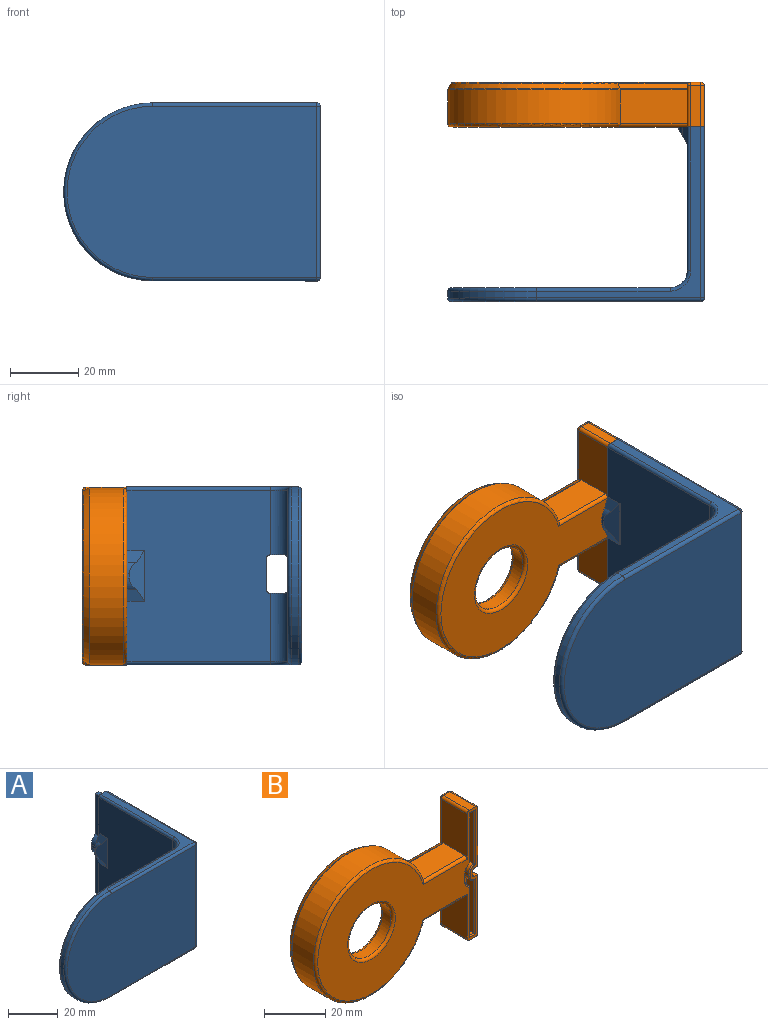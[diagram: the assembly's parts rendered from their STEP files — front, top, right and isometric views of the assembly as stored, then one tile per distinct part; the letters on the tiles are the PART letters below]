
ASSEMBLY  parts=2 mates=1
PART A: 74 faces, bbox 77.1x54.4x56.3 mm
  f0: plane 50x50mm, normal (1,0,0), area 2292.3mm2, adj f2,f6,f7,f11,f12,f13,f14,f18
  f1: plane 50x42mm, normal (-1,0,0), area 2013.4mm2, adj f11,f12,f13,f19,f22,f23,f24,f41
  f2: plane 74x50mm, normal (0,1,0), area 3023.7mm2, adj f0,f20,f21,f44,f45,f49,f50,f51
  f3: plane 73x50mm, normal (0,-1,0), area 3381.7mm2, adj f56,f57,f59,f61
  f4: plane 50x48mm, normal (0,0,1), area 247.7mm2, adj f23,f46,f47,f48,f49,f54,f56
  f5: plane 50x48mm, normal (0,0,-1), area 247.7mm2, adj f23,f46,f51,f52,f53,f58,f61
  f6: plane 39.8x1.5mm, normal (0,0,1), area 59.7mm2, adj f0,f10,f18,f23
  f7: plane 39.8x1.5mm, normal (0,0,-1), area 59.7mm2, adj f0,f9,f14,f23
  f8: plane 39.8x1.4mm, normal (1,0,0), area 55.7mm2, adj f9,f10,f16,f23
  f9: cylinder r=1mm len=39.8mm, axis (0,-1,0), area 62.5mm2, adj f7,f8,f15,f23
  f10: cylinder r=1mm len=39.8mm, axis (0,1,0), area 62.5mm2, adj f6,f8,f17,f23
  f11: plane 7x4.2mm, normal (0,0,1), area 23.4mm2, adj f0,f1,f19,f20,f44
  f12: plane 7x4.2mm, normal (0,0,-1), area 23.4mm2, adj f0,f1,f21,f22,f45
  f13: plane 9.2x5mm, normal (0,-1,0), area 28.8mm2, adj f0,f1,f14,f15,f16,f17,f18,f19
  f14: cylinder r=1mm len=1.5mm, axis (-1,0,0), area 2.4mm2, adj f0,f7,f13,f15
  f15: torus R=2mm, axis (0,1,0), area 3.4mm2, adj f9,f13,f14,f16
  f16: cylinder r=1mm len=1.4mm, axis (0,0,-1), area 2.2mm2, adj f8,f13,f15,f17
  f17: torus R=2mm, axis (0,1,0), area 3.4mm2, adj f10,f13,f16,f18
  f18: cylinder r=1mm len=1.5mm, axis (1,0,0), area 2.4mm2, adj f0,f6,f13,f17
  f19: cylinder r=1mm len=5mm, axis (1,0,0), area 7.9mm2, adj f0,f1,f11,f13
  f20: cylinder r=1mm len=10mm, axis (1,0,0), area 13.2mm2, adj f0,f2,f11,f44
  f21: cylinder r=1mm len=10mm, axis (-1,0,0), area 13.2mm2, adj f0,f2,f12,f45
  f22: cylinder r=1mm len=5mm, axis (-1,0,0), area 7.9mm2, adj f0,f1,f12,f13
  f23: plane 52x7.5mm, normal (0,1,0), area 138.1mm2, adj f0,f1,f4,f5,f6,f7,f8,f9
  f24: plane 14.72x0.02mm, normal (0,-1,0), area 0.3mm2, adj f1,f41,f42,f43
  f25: plane 1.34x0.7mm, normal (-1,0,0), area 0.9mm2, adj f23,f39,f40,f43
  f26: cylinder r=2.6mm len=3mm, axis (0,-1,0), area 12mm2, adj f27,f37,f38,f73
  f27: plane 3x1.4mm, normal (1,0,0), area 4.2mm2, adj f26,f28,f38,f71
  f28: cylinder r=2.6mm len=3mm, axis (0,-1,0), area 12mm2, adj f27,f29,f38,f69
  f29: plane 21.1x3mm, normal (1,0,0), area 63.3mm2, adj f28,f30,f38,f67
  f30: plane 3x1.8mm, normal (0,0,-1), area 5.4mm2, adj f29,f31,f38,f65
  f31: plane 19.83x3mm, normal (-1,0,0), area 59.5mm2, adj f30,f32,f38,f63
  f32: cylinder r=4.4mm len=3.97mm, axis (0,-1,0), area 14.8mm2, adj f31,f33,f38,f62
  f33: plane 3x1.2mm, normal (-1,0,0), area 3.6mm2, adj f32,f34,f38,f64
  f34: cylinder r=4.4mm len=3.97mm, axis (0,-1,0), area 14.8mm2, adj f33,f35,f38,f66
  f35: plane 19.83x3mm, normal (-1,0,0), area 59.5mm2, adj f34,f36,f38,f68
  f36: plane 3x1.8mm, normal (0,0,1), area 5.4mm2, adj f35,f37,f38,f70
  f37: plane 21.1x3mm, normal (1,0,0), area 63.3mm2, adj f26,f36,f38,f72
  f38: plane 48.8x4.3mm, normal (0,1,0), area 91.5mm2, adj f26,f27,f28,f29,f30,f31,f32,f33
  f39: cylinder r=5mm len=3.28mm, axis (0,-1,0), area 5.1mm2, adj f23,f25,f41,f43
  f40: cylinder r=5mm len=3.28mm, axis (0,-1,0), area 5.1mm2, adj f23,f25,f42,f43
  f41: plane 5x3.41mm, normal (-0.94,0,0.35), area 14.3mm2, adj f1,f23,f24,f39,f43
  f42: plane 5x3.41mm, normal (-0.94,0,-0.35), area 14.3mm2, adj f1,f23,f24,f40,f43
  f43: plane 14.62x4.3mm, normal (-0.87,-0.5,0), area 42.6mm2, adj f24,f25,f39,f40,f41,f42
  f44: cylinder r=5mm len=20.9mm, axis (0,0,1), area 157.5mm2, adj f1,f2,f11,f20,f52
  f45: cylinder r=5mm len=19.9mm, axis (0,0,1), area 149.7mm2, adj f1,f2,f12,f21,f48
  f46: cylinder r=26mm len=52mm, axis (0,1,0), area 163.4mm2, adj f4,f5,f50,f59
  f47: cylinder r=1mm len=42mm, axis (0,1,0), area 66mm2, adj f1,f4,f23,f48
  f48: torus R=6mm, axis (0,0,1), area 13.2mm2, adj f4,f45,f47,f49
  f49: cylinder r=1mm len=39mm, axis (1,0,0), area 61.3mm2, adj f2,f4,f48,f50
  f50: torus R=25mm, axis (0,-1,0), area 126.5mm2, adj f2,f46,f49,f51
  f51: cylinder r=1mm len=39mm, axis (-1,0,0), area 61.3mm2, adj f2,f5,f50,f52
  f52: torus R=6mm, axis (0,0,1), area 13.2mm2, adj f5,f44,f51,f53
  f53: cylinder r=1mm len=42mm, axis (0,-1,0), area 66mm2, adj f1,f5,f23,f52
  f54: cylinder r=1mm len=50mm, axis (0,-1,0), area 78.5mm2, adj f0,f4,f23,f55
  f55: sphere r=1mm, area 1.6mm2, adj f54,f56,f57
  f56: cylinder r=1mm len=48mm, axis (-1,0,0), area 75.4mm2, adj f3,f4,f55,f59
  f57: cylinder r=1mm len=50mm, axis (0,0,-1), area 78.5mm2, adj f0,f3,f55,f60
  f58: cylinder r=1mm len=50mm, axis (0,1,0), area 78.5mm2, adj f0,f5,f23,f60
  f59: torus R=25mm, axis (0,1,0), area 126.5mm2, adj f3,f46,f56,f61
  f60: sphere r=1mm, area 1.6mm2, adj f57,f58,f61
  f61: cylinder r=1mm len=48mm, axis (1,0,0), area 75.4mm2, adj f3,f5,f59,f60
  f62: torus R=4.8mm, axis (0,-1,0), area 3.1mm2, adj f23,f32,f63,f64
  f63: cylinder r=0.4mm len=20.23mm, axis (0,0,-1), area 12.5mm2, adj f23,f31,f62,f65
  f64: cylinder r=0.4mm len=1.2mm, axis (0,0,-1), area 0.8mm2, adj f23,f33,f62,f66
  f65: cylinder r=0.4mm len=2.6mm, axis (1,0,0), area 1.3mm2, adj f23,f30,f63,f67
  f66: torus R=4.8mm, axis (0,-1,0), area 3.1mm2, adj f23,f34,f64,f68
  f67: cylinder r=0.4mm len=21.92mm, axis (0,0,1), area 13.4mm2, adj f23,f29,f65,f69
  f68: cylinder r=0.4mm len=20.23mm, axis (0,0,-1), area 12.5mm2, adj f23,f35,f66,f70
  f69: torus R=2.2mm, axis (0,-1,0), area 2.5mm2, adj f23,f28,f67,f71
  f70: cylinder r=0.4mm len=2.6mm, axis (-1,0,0), area 1.3mm2, adj f23,f36,f68,f72
  f71: cylinder r=0.4mm len=1.4mm, axis (0,0,1), area 0.9mm2, adj f23,f27,f69,f73
  f72: cylinder r=0.4mm len=21.92mm, axis (0,0,1), area 13.4mm2, adj f23,f37,f70,f73
  f73: torus R=2.2mm, axis (0,-1,0), area 2.5mm2, adj f23,f26,f71,f72
PART B: 93 faces, bbox 79.4x13.1x56 mm
  f0: plane 23.3x12mm, normal (1,0,0), area 237.5mm2, adj f7,f14,f23,f60,f63,f65,f66
  f1: plane 23.3x12mm, normal (1,0,0), area 237.5mm2, adj f6,f14,f22,f51,f53,f55,f56
  f2: plane 12x3mm, normal (0,0,-1), area 36mm2, adj f14,f48,f50,f51
  f3: plane 12x3mm, normal (0,0,1), area 36mm2, adj f14,f57,f60,f61
  f4: plane 18x12mm, normal (-1,0,0), area 204.5mm2, adj f14,f19,f57,f58,f67,f84,f87
  f5: plane 18x12mm, normal (-1,0,0), area 204.5mm2, adj f14,f20,f47,f48,f69,f86,f88
  f6: plane 5x1.67mm, normal (0,0,1), area 5.8mm2, adj f1,f10,f14,f22,f29
  f7: plane 5x1.67mm, normal (0,0,-1), area 5.8mm2, adj f0,f9,f14,f23,f28
  f8: plane 4x1.4mm, normal (1,0,0), area 5.6mm2, adj f9,f10,f14,f21
  f9: cylinder r=1mm len=4mm, axis (0,-1,0), area 6.3mm2, adj f7,f8,f14,f28
  f10: cylinder r=1mm len=4mm, axis (0,1,0), area 6.3mm2, adj f6,f8,f14,f29
  f11: plane 72.61x50mm, normal (0,1,0), area 263.8mm2, adj f30,f31,f32,f47,f50,f53,f58,f61
  f12: cylinder r=25.85mm len=51.7mm, axis (0,1,0), area 1445.9mm2, adj f19,f20,f68,f89
  f13: cylinder r=10mm len=20mm, axis (0,1,0), area 251.3mm2, adj f70,f71
  f14: plane 74x52mm, normal (0,-1,0), area 1940mm2, adj f0,f1,f2,f3,f4,f5,f6,f7
  f15: cylinder r=22.85mm len=45.7mm, axis (0,1,0), area 694.1mm2, adj f17,f18,f31,f33
  f16: plane 66.5x43.7mm, normal (0,1,0), area 1303.1mm2, adj f21,f22,f23,f24,f26,f33,f70
  f17: plane 25.85x6.46mm, normal (0,0,-1), area 135.8mm2, adj f15,f24,f25,f30,f65
  f18: plane 25.85x6.46mm, normal (0,0,1), area 135.8mm2, adj f15,f26,f27,f32,f55
  f19: plane 19.57x9.89mm, normal (0,0,1), area 193.6mm2, adj f4,f12,f67,f87
  f20: plane 19.57x9.89mm, normal (0,0,-1), area 193.6mm2, adj f5,f12,f69,f88
  f21: cylinder r=2mm len=2mm, axis (0,0,-1), area 4.4mm2, adj f8,f16,f28,f29
  f22: cylinder r=4.5mm len=4.5mm, axis (0,0,1), area 17.4mm2, adj f1,f6,f16,f27,f29
  f23: cylinder r=4.5mm len=4.5mm, axis (0,0,1), area 17.4mm2, adj f0,f7,f16,f25,f28
  f24: cylinder r=1mm len=23.17mm, axis (-1,0,0), area 35.6mm2, adj f16,f17,f25,f33
  f25: torus R=5.5mm, axis (0,0,1), area 8mm2, adj f17,f23,f24,f66
  f26: cylinder r=1mm len=23.17mm, axis (1,0,0), area 35.6mm2, adj f16,f18,f27,f33
  f27: torus R=5.5mm, axis (0,0,1), area 8mm2, adj f18,f22,f26,f56
  f28: torus R=3mm, axis (0,0,-1), area 3.2mm2, adj f7,f9,f21,f23
  f29: torus R=3mm, axis (0,0,-1), area 3.2mm2, adj f6,f10,f21,f22
  f30: cylinder r=0.8mm len=25.85mm, axis (-1,0,0), area 32.2mm2, adj f11,f17,f31,f64
  f31: torus R=23.65mm, axis (0,-1,0), area 169.3mm2, adj f11,f15,f30,f32
  f32: cylinder r=0.8mm len=25.85mm, axis (1,0,0), area 32.2mm2, adj f11,f18,f31,f54
  f33: torus R=21.85mm, axis (0,1,0), area 207.3mm2, adj f15,f16,f24,f26
  f34: plane 21.3x3.3mm, normal (-1,0,0), area 70.3mm2, adj f35,f45,f46,f73
  f35: cylinder r=2.5mm len=3.3mm, axis (0,-1,0), area 13mm2, adj f34,f36,f46,f72
  f36: plane 3.3x1.4mm, normal (-1,0,0), area 4.6mm2, adj f35,f37,f46,f74
  f37: cylinder r=2.5mm len=3.3mm, axis (0,-1,0), area 13mm2, adj f36,f38,f46,f76
  f38: plane 21.3x3.3mm, normal (-1,0,0), area 70.3mm2, adj f37,f39,f46,f78
  f39: plane 3.3x2mm, normal (0,0,-1), area 6.6mm2, adj f38,f40,f46,f80
  f40: plane 19.77x3.3mm, normal (1,0,0), area 65.2mm2, adj f39,f41,f46,f82
  f41: cylinder r=4.5mm len=4.03mm, axis (0,-1,0), area 16.5mm2, adj f40,f42,f46,f83
  f42: plane 3.3x1.3mm, normal (1,0,0), area 4.3mm2, adj f41,f43,f46,f81
  f43: cylinder r=4.5mm len=4.03mm, axis (0,-1,0), area 16.5mm2, adj f42,f44,f46,f79
  f44: plane 19.87x3.3mm, normal (1,0,0), area 65.6mm2, adj f43,f45,f46,f77
  f45: plane 3.3x2mm, normal (0,0,1), area 6.6mm2, adj f34,f44,f46,f75
  f46: plane 49x4.5mm, normal (0,-1,0), area 102.4mm2, adj f34,f35,f36,f37,f38,f39,f40,f41
  f47: cylinder r=1mm len=18.39mm, axis (0,0,1), area 28.2mm2, adj f5,f11,f49,f86,f92
  f48: cylinder r=1mm len=12mm, axis (0,-1,0), area 18.8mm2, adj f2,f5,f14,f49
  f49: sphere r=1mm, area 1.6mm2, adj f47,f48,f50
  f50: cylinder r=1mm len=3mm, axis (-1,0,0), area 4.7mm2, adj f2,f11,f49,f52
  f51: cylinder r=1mm len=12mm, axis (0,1,0), area 18.8mm2, adj f1,f2,f14,f52
  f52: sphere r=1mm, area 1.6mm2, adj f50,f51,f53
  f53: cylinder r=1mm len=19.2mm, axis (0,0,-1), area 30mm2, adj f1,f11,f52,f54
  f54: bspline ~1.23x1mm, area 1.3mm2, adj f32,f53,f55
  f55: cylinder r=1mm len=6.46mm, axis (0,1,0), area 10mm2, adj f1,f18,f54,f56
  f56: bspline ~4.24x2mm, area 3.6mm2, adj f1,f27,f55
  f57: cylinder r=1mm len=12mm, axis (0,1,0), area 18.8mm2, adj f3,f4,f14,f59
  f58: cylinder r=1mm len=18.39mm, axis (0,0,-1), area 28.2mm2, adj f4,f11,f59,f84,f90
  f59: sphere r=1mm, area 1.6mm2, adj f57,f58,f61
  f60: cylinder r=1mm len=12mm, axis (0,-1,0), area 18.8mm2, adj f0,f3,f14,f62
  f61: cylinder r=1mm len=3mm, axis (1,0,0), area 4.7mm2, adj f3,f11,f59,f62
  f62: sphere r=1mm, area 1.6mm2, adj f60,f61,f63
  f63: cylinder r=1mm len=19.2mm, axis (0,0,-1), area 30mm2, adj f0,f11,f62,f64
  f64: bspline ~1.23x1mm, area 1.3mm2, adj f30,f63,f65
  f65: cylinder r=1mm len=6.46mm, axis (0,-1,0), area 10mm2, adj f0,f17,f64,f66
  f66: bspline ~4.24x2mm, area 3.6mm2, adj f0,f25,f65
  f67: cylinder r=1mm len=20.31mm, axis (1,0,0), area 31.2mm2, adj f4,f14,f19,f68
  f68: torus R=24.85mm, axis (0,-1,0), area 227.2mm2, adj f12,f14,f67,f69
  f69: cylinder r=1mm len=20.31mm, axis (1,0,0), area 31.2mm2, adj f5,f14,f20,f68
  f70: torus R=11mm, axis (0,1,0), area 102.3mm2, adj f13,f16
  f71: torus R=11mm, axis (0,-1,0), area 102.3mm2, adj f13,f14
  f72: torus R=2.1mm, axis (0,-1,0), area 2.5mm2, adj f14,f35,f73,f74
  f73: cylinder r=0.4mm len=22.14mm, axis (0,0,-1), area 13.6mm2, adj f14,f34,f72,f75
  f74: cylinder r=0.4mm len=1.4mm, axis (0,0,-1), area 0.9mm2, adj f14,f36,f72,f76
  f75: cylinder r=0.4mm len=2.8mm, axis (-1,0,0), area 1.5mm2, adj f14,f45,f73,f77
  f76: torus R=2.1mm, axis (0,-1,0), area 2.5mm2, adj f14,f37,f74,f78
  f77: cylinder r=0.4mm len=20.27mm, axis (0,0,1), area 12.5mm2, adj f14,f44,f75,f79
  f78: cylinder r=0.4mm len=22.14mm, axis (0,0,-1), area 13.6mm2, adj f14,f38,f76,f80
  f79: torus R=4.9mm, axis (0,-1,0), area 3.2mm2, adj f14,f43,f77,f81
  f80: cylinder r=0.4mm len=2.8mm, axis (1,0,0), area 1.5mm2, adj f14,f39,f78,f82
  f81: cylinder r=0.4mm len=1.3mm, axis (0,0,1), area 0.8mm2, adj f14,f42,f79,f83
  f82: cylinder r=0.4mm len=20.17mm, axis (0,0,1), area 12.5mm2, adj f14,f40,f80,f83
  f83: torus R=4.9mm, axis (0,-1,0), area 3.2mm2, adj f14,f41,f81,f82
  f84: plane 20.79x1.76mm, normal (0,0.5,0.87), area 39.5mm2, adj f4,f58,f85,f87,f90
  f85: cone r=25.85mm half-angle=30deg, axis (0,-1,0), area 283.6mm2, adj f84,f86,f89,f91
  f86: plane 20.79x1.76mm, normal (0,0.5,-0.87), area 39.5mm2, adj f5,f47,f85,f88,f92
  f87: cylinder r=0.4mm len=19.61mm, axis (-1,0,0), area 4.1mm2, adj f4,f19,f84,f89
  f88: cylinder r=0.4mm len=19.61mm, axis (1,0,0), area 4.1mm2, adj f5,f20,f86,f89
  f89: torus R=25.45mm, axis (0,1,0), area 30.6mm2, adj f12,f85,f87,f88
  f90: cylinder r=0.4mm len=21.6mm, axis (-1,0,0), area 8.9mm2, adj f11,f58,f84,f91
  f91: torus R=24.46mm, axis (0,-1,0), area 59.1mm2, adj f11,f85,f90,f92
  f92: cylinder r=0.4mm len=21.6mm, axis (1,0,0), area 8.9mm2, adj f11,f47,f86,f91
PLACE A t=(-30.27,20.44,-8.41)mm
PLACE B t=(-30.27,20.44,-8.51)mm
MATE planar A.f23 <-> B.f14  axis (0,1,0) through (44.73,9.44,4.24)mm
